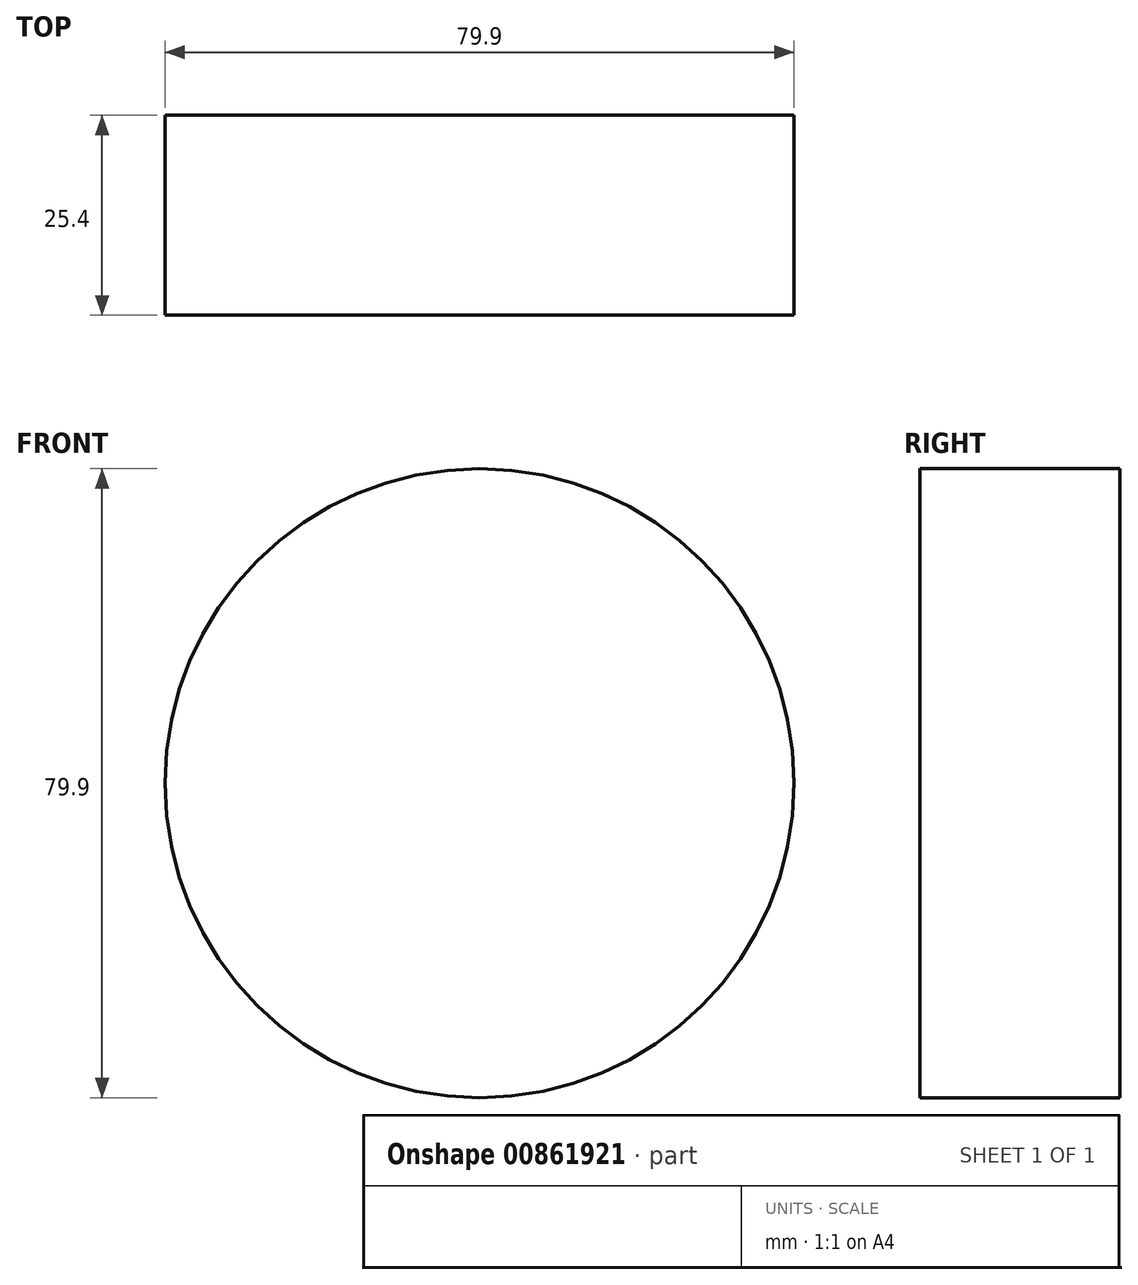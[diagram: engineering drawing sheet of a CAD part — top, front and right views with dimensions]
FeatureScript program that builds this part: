
annotation { "Feature Type Name" : "Feature", "Feature Type Description" : "" }
export const myFeature = defineFeature(function(context is Context, id is Id, definition is map)
    precondition{}
    {
        {
            var Q0;
            Q0=qCreatedBy(makeId("Front.planeOp"),FACE);
            var sketch = newSketch(context, id + "F0", { "sketchPlane" : qUnion([Q0])});
            skCircle(sketch, "E0", {"center": v(0, 0) * mm, "radius": 38.16 * mm});
            skCircle(sketch, "E1", {"center": v(0, 0) * mm, "radius": 39.95 * mm});
            skSolve(sketch);
        }
        {
            var Q0;
            Q0=makeQuery(id+"F0.imprint","IMPRINT",FACE,{"disambiguationData":[TD([[makeQuery(id+"F0.imprint","IMPRINT",EDGE,{"derivedFrom":sQuery(id+"F0.wireOp",EDGE,"E0")}),-1.0]])]});
            var Q1;
            Q1=makeQuery(id+"F0.imprint","IMPRINT",FACE,{"disambiguationData":[TD([[makeQuery(id+"F0.imprint","IMPRINT",EDGE,{"derivedFrom":sQuery(id+"F0.wireOp",EDGE,"E0")}),1.0]])]});
            extrude(context, id + "F1", {"entities" : qUnion([Q0, Q1]), "depth" : 25.4 * mm, "offsetDistance" : 25.4 * mm});
        }
    });
